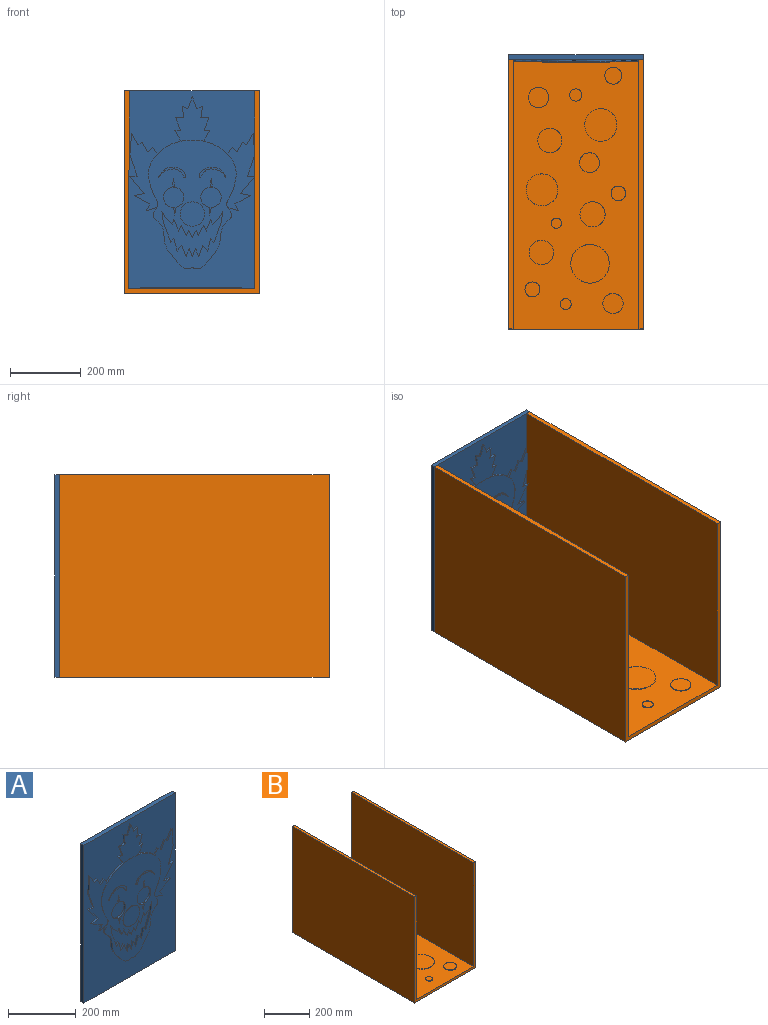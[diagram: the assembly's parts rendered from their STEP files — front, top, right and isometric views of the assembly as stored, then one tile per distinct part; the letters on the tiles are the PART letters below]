
ASSEMBLY  parts=2 mates=1
PART A: 117 faces, bbox 381x20.3x571.5 mm
  f0: plane 571.5x381mm, normal (0,-1,0), area 127557.7mm2, adj f1,f2,f3,f4,f37,f40,f42,f43
  f1: plane 381x12.7mm, normal (0,0,1), area 4838.7mm2, adj f0,f2,f4,f5
  f2: plane 571.5x12.7mm, normal (-1,0,0), area 7258mm2, adj f0,f1,f3,f5
  f3: plane 381x12.7mm, normal (0,0,-1), area 4838.7mm2, adj f0,f2,f4,f5
  f4: plane 571.5x12.7mm, normal (1,0,0), area 7258mm2, adj f0,f1,f3,f5
  f5: plane 571.5x381mm, normal (0,1,0), area 217741.5mm2, adj f1,f2,f3,f4
  f6: plane 19.84x18.99mm, normal (0.69,0,-0.72), area 174.4mm2, adj f7,f47,f48,f63
  f7: plane 17.73x9.29mm, normal (0.89,0,-0.46), area 127.1mm2, adj f6,f8,f48,f63
  f8: plane 32.08x6.35mm, normal (-0.99,0,0.12), area 205.1mm2, adj f7,f9,f48,f63
  f9: plane 56.13x21.1mm, normal (-0.94,0,0.35), area 380.8mm2, adj f8,f10,f48,f63
  f10: plane 10.13x8.86mm, normal (0.75,0,0.66), area 85.5mm2, adj f9,f11,f48,f63
  f11: plane 35.03x8.86mm, normal (-0.97,0,0.25), area 229.5mm2, adj f10,f12,f48,f63
  f12: plane 16.88x13.51mm, normal (0.78,0,0.62), area 137.3mm2, adj f11,f13,f48,f63
  f13: plane 32.5x11.82mm, normal (-0.94,0,0.34), area 219.6mm2, adj f12,f14,f48,f63
  f14: plane 22.37x8.44mm, normal (0.94,0,0.35), area 151.8mm2, adj f13,f15,f48,f63
  f15: plane 23.21x9.37mm, normal (-0.93,0,0.37), area 159mm2, adj f14,f16,f48,f63
  f16: plane 23.21x9.37mm, normal (0.93,0,0.37), area 159mm2, adj f15,f17,f48,f63
  f17: plane 22.37x8.44mm, normal (-0.94,0,0.35), area 151.8mm2, adj f16,f18,f48,f63
  f18: plane 32.5x11.82mm, normal (0.94,0,0.34), area 219.6mm2, adj f17,f19,f48,f63
  f19: plane 16.88x13.51mm, normal (-0.78,0,0.62), area 137.3mm2, adj f18,f20,f48,f63
  f20: plane 35.03x8.86mm, normal (0.97,0,0.25), area 229.5mm2, adj f19,f21,f48,f63
  f21: plane 10.13x8.86mm, normal (-0.75,0,0.66), area 85.5mm2, adj f20,f22,f48,f63
  f22: plane 56.13x21.1mm, normal (0.94,0,0.35), area 380.8mm2, adj f21,f23,f48,f63
  f23: plane 32.08x6.35mm, normal (0.99,0,0.12), area 205.1mm2, adj f22,f24,f48,f63
  f24: plane 17.73x9.29mm, normal (-0.89,0,-0.46), area 127.1mm2, adj f23,f25,f48,f63
  f25: plane 19.84x18.99mm, normal (-0.69,0,-0.72), area 174.4mm2, adj f24,f26,f48,f63
  f26: plane 13.96x6.35mm, normal (0.95,0,-0.32), area 93.7mm2, adj f25,f27,f48,f63
  f27: plane 33.84x12.78mm, normal (-0.94,0,-0.35), area 229.7mm2, adj f26,f28,f48,f63
  f28: plane 16.54x7.52mm, normal (0.91,0,-0.41), area 115.4mm2, adj f27,f29,f48,f63
  f29: plane 30.08x14.29mm, normal (-0.9,0,-0.43), area 211.5mm2, adj f28,f30,f48,f63
  f30: plane 15.79x6.77mm, normal (0.92,0,-0.39), area 109.1mm2, adj f29,f31,f48,f63
  f31: plane 20.3x10.51mm, normal (-0.89,0,-0.46), area 145.2mm2, adj f30,f32,f48,f63
  f32: plane 20.3x10.51mm, normal (0.89,0,-0.46), area 145.2mm2, adj f31,f33,f48,f63
  f33: plane 15.79x6.77mm, normal (-0.92,0,-0.39), area 109.1mm2, adj f32,f34,f48,f63
  f34: plane 30.08x14.29mm, normal (0.9,0,-0.43), area 211.5mm2, adj f33,f35,f48,f63
  f35: plane 16.54x7.52mm, normal (-0.91,0,-0.41), area 115.4mm2, adj f34,f36,f48,f63
  f36: plane 33.84x12.78mm, normal (0.94,0,-0.35), area 229.7mm2, adj f35,f47,f48,f63
  f37: extruded ~67.83x36.44mm, area 496.6mm2, adj f0,f38,f46,f48,f75,f104
  f38: extruded ~31.62x2.5mm, area 40.4mm2, adj f37,f39,f48,f88
  f39: extruded ~31.62x2.5mm, area 40.4mm2, adj f38,f40,f48,f88
  f40: extruded ~67.83x36.44mm, area 496.6mm2, adj f0,f39,f41,f48,f74,f89
  f41: extruded ~151.17x26.58mm, area 207.7mm2, adj f40,f42,f48,f102
  f42: extruded ~173.03x111.11mm, area 1449.8mm2, adj f0,f41,f43,f48,f101
  f43: extruded ~173.03x111.11mm, area 1449.8mm2, adj f0,f42,f46,f48,f105
  f44: cylinder r=28.78mm len=57.56mm, axis (0,1,0), area 1148.3mm2, adj f48,f65
  f45: cylinder r=28.78mm len=57.56mm, axis (0,1,0), area 1148.3mm2, adj f48,f64
  f46: extruded ~151.17x26.58mm, area 207.7mm2, adj f37,f43,f48,f116
  f47: plane 13.96x6.35mm, normal (-0.95,0,-0.32), area 93.7mm2, adj f6,f36,f48,f63
  f48: plane 367.53x249.86mm, normal (0,-1,0), area 47753.7mm2, adj f6,f7,f8,f9,f10,f11,f12,f13
  f49: plane 21.89x5.73mm, normal (0,-1,0), area 61.6mm2, adj f50,f51,f52
  f50: plane 21.22x2.46mm, normal (0.99,0,0.12), area 27.1mm2, adj f48,f49,f51,f52
  f51: plane 5.73x1.27mm, normal (0.12,0,-0.99), area 7.3mm2, adj f48,f49,f50,f52
  f52: plane 21.89x3.27mm, normal (-0.99,0,0.15), area 28.1mm2, adj f48,f49,f50,f51
  f53: plane 18.6x4.65mm, normal (0,-1,0), area 42.8mm2, adj f54,f55,f56
  f54: plane 18.6x1.27mm, normal (1,0,-0.06), area 23.7mm2, adj f48,f53,f55,f56
  f55: plane 17.91x3.48mm, normal (-0.98,0,-0.19), area 23.2mm2, adj f48,f53,f54,f56
  f56: plane 4.65x1.27mm, normal (-0.15,0,0.99), area 6mm2, adj f48,f53,f54,f55
  f57: plane 21.89x5.73mm, normal (0,-1,0), area 61.6mm2, adj f58,f59,f60
  f58: plane 5.73x1.27mm, normal (-0.12,0,-0.99), area 7.3mm2, adj f48,f57,f59,f60
  f59: plane 21.22x2.46mm, normal (-0.99,0,0.12), area 27.1mm2, adj f48,f57,f58,f60
  f60: plane 21.89x3.27mm, normal (0.99,0,0.15), area 28.1mm2, adj f48,f57,f58,f59
  f61: plane 69.41x69.41mm, normal (0,-1,0), area 3784.2mm2, adj f62
  f62: cylinder r=34.71mm len=69.41mm, axis (0,1,0), area 276.9mm2, adj f48,f61
  f63: plane 171.53x129.57mm, normal (0,-1,0), area 8466.9mm2, adj f6,f7,f8,f9,f10,f11,f12,f13
  f64: plane 57.56x57.56mm, normal (0,-1,0), area 2602.1mm2, adj f45
  f65: plane 57.56x57.56mm, normal (0,-1,0), area 2602.1mm2, adj f44
  f66: plane 77.58x32.72mm, normal (0,-1,0), area 463.6mm2, adj f67
  f67: extruded ~75.23x29.94mm, area 252.3mm2, adj f48,f66
  f68: plane 77.58x32.72mm, normal (0,-1,0), area 464.8mm2, adj f69
  f69: extruded ~75.23x29.94mm, area 252.3mm2, adj f48,f68
  f70: plane 18.6x4.65mm, normal (0,-1,0), area 42.8mm2, adj f71,f72,f73
  f71: plane 4.65x1.27mm, normal (0.15,0,0.99), area 6mm2, adj f48,f70,f72,f73
  f72: plane 17.91x3.48mm, normal (0.98,0,-0.19), area 23.2mm2, adj f48,f70,f71,f73
  f73: plane 18.6x1.27mm, normal (-1,0,-0.06), area 23.7mm2, adj f48,f70,f71,f72
  f74: plane 30.2x18.01mm, normal (-0.86,0,-0.51), area 178.6mm2, adj f0,f40,f87,f88
  f75: plane 30.2x18.01mm, normal (0.86,0,-0.51), area 178.6mm2, adj f0,f37,f76,f88
  f76: plane 16.18x5.08mm, normal (0,0,1), area 82.2mm2, adj f0,f75,f77,f88
  f77: plane 36.03x13.54mm, normal (0.94,0,-0.35), area 195.5mm2, adj f0,f76,f78,f88
  f78: plane 22.94x5.08mm, normal (0,0,1), area 116.5mm2, adj f0,f77,f79,f88
  f79: plane 32.34x5.08mm, normal (0.99,0,-0.15), area 166.1mm2, adj f0,f78,f80,f88
  f80: plane 16.54x6.77mm, normal (-0.38,0,0.93), area 90.8mm2, adj f0,f79,f81,f88
  f81: plane 33.46x12.39mm, normal (0.94,0,0.35), area 181.3mm2, adj f0,f80,f82,f88
  f82: plane 33.46x12.39mm, normal (-0.94,0,0.35), area 181.3mm2, adj f0,f81,f83,f88
  f83: plane 16.54x6.77mm, normal (0.38,0,0.93), area 90.8mm2, adj f0,f82,f84,f88
  f84: plane 32.34x5.08mm, normal (-0.99,0,-0.15), area 166.1mm2, adj f0,f83,f85,f88
  f85: plane 22.94x5.08mm, normal (0,0,1), area 116.5mm2, adj f0,f84,f86,f88
  f86: plane 36.03x13.54mm, normal (-0.94,0,-0.35), area 195.5mm2, adj f0,f85,f87,f88
  f87: plane 16.18x5.08mm, normal (0,0,1), area 82.2mm2, adj f0,f74,f86,f88
  f88: plane 125.26x99.25mm, normal (0,-1,0), area 7084.9mm2, adj f38,f39,f74,f75,f76,f77,f78,f79
  f89: plane 17.86x12.83mm, normal (0.81,0,0.58), area 111.7mm2, adj f0,f40,f90,f102
  f90: plane 14.6x11.87mm, normal (-0.63,0,0.78), area 95.6mm2, adj f0,f89,f91,f102
  f91: plane 27.04x14.65mm, normal (0.88,0,0.48), area 156.2mm2, adj f0,f90,f92,f102
  f92: plane 12.52x6.78mm, normal (-0.48,0,0.88), area 72.3mm2, adj f0,f91,f93,f102
  f93: plane 32.81x17.77mm, normal (0.88,0,0.48), area 189.6mm2, adj f0,f92,f94,f102
  f94: plane 61.52x5.08mm, normal (-1,0,0.08), area 313.4mm2, adj f0,f93,f95,f102
  f95: plane 59.72x20.28mm, normal (-0.95,0,-0.32), area 320.4mm2, adj f0,f94,f96,f102
  f96: plane 20.85x5.08mm, normal (0,0,1), area 105.9mm2, adj f0,f95,f97,f102
  f97: plane 49.58x41.13mm, normal (-0.77,0,-0.64), area 327.2mm2, adj f0,f96,f98,f102
  f98: plane 28.73x5.63mm, normal (-0.19,0,0.98), area 148.7mm2, adj f0,f97,f99,f102
  f99: plane 44.51x23.66mm, normal (-0.47,0,-0.88), area 256.1mm2, adj f0,f98,f100,f102
  f100: plane 18.9x10.05mm, normal (-0.88,0,0.47), area 108.8mm2, adj f0,f99,f101,f102
  f101: plane 29.51x8.79mm, normal (0.29,0,-0.96), area 156.4mm2, adj f0,f42,f100,f102
  f102: plane 219.02x81.12mm, normal (0,-1,0), area 8377.8mm2, adj f41,f89,f90,f91,f92,f93,f94,f95
  f103: plane 14.6x11.87mm, normal (0.63,0,0.78), area 95.6mm2, adj f0,f104,f115,f116
  f104: plane 17.86x12.83mm, normal (-0.81,0,0.58), area 111.7mm2, adj f0,f37,f103,f116
  f105: plane 29.51x8.79mm, normal (-0.29,0,-0.96), area 156.4mm2, adj f0,f43,f106,f116
  f106: plane 18.9x10.05mm, normal (0.88,0,0.47), area 108.8mm2, adj f0,f105,f107,f116
  f107: plane 44.51x23.66mm, normal (0.47,0,-0.88), area 256.1mm2, adj f0,f106,f108,f116
  f108: plane 28.73x5.63mm, normal (0.19,0,0.98), area 148.7mm2, adj f0,f107,f109,f116
  f109: plane 49.58x41.13mm, normal (0.77,0,-0.64), area 327.2mm2, adj f0,f108,f110,f116
  f110: plane 20.85x5.08mm, normal (0,0,1), area 105.9mm2, adj f0,f109,f111,f116
  f111: plane 59.72x20.28mm, normal (0.95,0,-0.32), area 320.4mm2, adj f0,f110,f112,f116
  f112: plane 61.52x5.08mm, normal (1,0,0.08), area 313.4mm2, adj f0,f111,f113,f116
  f113: plane 32.81x17.77mm, normal (-0.88,0,0.48), area 189.6mm2, adj f0,f112,f114,f116
  f114: plane 12.52x6.78mm, normal (0.48,0,0.88), area 72.3mm2, adj f0,f113,f115,f116
  f115: plane 27.04x14.65mm, normal (-0.88,0,0.48), area 156.2mm2, adj f0,f103,f114,f116
  f116: plane 219.02x81.12mm, normal (0,-1,0), area 8377.5mm2, adj f46,f103,f104,f105,f106,f107,f108,f109
PART B: 40 faces, bbox 381x762x571.5 mm
  f0: plane 762x12.7mm, normal (0,0,1), area 9677.4mm2, adj f1,f7,f8,f9
  f1: plane 762x571.5mm, normal (-1,0,0), area 435483mm2, adj f0,f2,f8,f9
  f2: plane 762x381mm, normal (0,0,-1), area 290322mm2, adj f1,f3,f8,f9
  f3: plane 762x571.5mm, normal (1,0,0), area 435483mm2, adj f2,f4,f8,f9
  f4: plane 762x12.7mm, normal (0,0,1), area 9677.4mm2, adj f3,f5,f8,f9
  f5: plane 762x558.8mm, normal (-1,0,0), area 425805.9mm2, adj f4,f6,f8,f9
  f6: plane 762x355.6mm, normal (0,0,1), area 222928.4mm2, adj f5,f7,f8,f9,f10,f12,f14,f16
  f7: plane 762x558.8mm, normal (1,0,0), area 425805.9mm2, adj f0,f6,f8,f9
  f8: plane 571.5x381mm, normal (0,1,0), area 19032.2mm2, adj f0,f1,f2,f3,f4,f5,f6,f7
  f9: plane 571.5x381mm, normal (0,-1,0), area 19032.2mm2, adj f0,f1,f2,f3,f4,f5,f6,f7
  f10: cylinder r=28.56mm len=57.12mm, axis (0,0,-1), area 455.8mm2, adj f6,f11
  f11: plane 57.12x57.12mm, normal (0,0,1), area 2562.1mm2, adj f10
  f12: cylinder r=45.7mm len=91.4mm, axis (0,0,-1), area 729.4mm2, adj f6,f13
  f13: plane 91.4x91.4mm, normal (0,0,1), area 6561.8mm2, adj f12
  f14: cylinder r=23.64mm len=47.28mm, axis (0,0,-1), area 377.3mm2, adj f6,f15
  f15: plane 47.28x47.28mm, normal (0,0,1), area 1756mm2, adj f14
  f16: cylinder r=34.24mm len=68.48mm, axis (0,0,-1), area 546.4mm2, adj f6,f17
  f17: plane 68.48x68.48mm, normal (0,0,1), area 3683.1mm2, adj f16
  f18: cylinder r=27.91mm len=55.82mm, axis (0,0,-1), area 445.4mm2, adj f6,f19
  f19: plane 55.82x55.82mm, normal (0,0,1), area 2447mm2, adj f18
  f20: cylinder r=45mm len=90mm, axis (0,0,-1), area 718.2mm2, adj f6,f21
  f21: plane 90x90mm, normal (0,0,1), area 6362.2mm2, adj f20
  f22: cylinder r=20.62mm len=41.24mm, axis (0,0,-1), area 329.1mm2, adj f6,f23
  f23: plane 41.24x41.24mm, normal (0,0,1), area 1335.7mm2, adj f22
  f24: cylinder r=35.53mm len=71.07mm, axis (0,0,-1), area 567.1mm2, adj f6,f25
  f25: plane 71.07x71.07mm, normal (0,0,1), area 3967mm2, adj f24
  f26: cylinder r=14.39mm len=28.78mm, axis (0,0,-1), area 229.7mm2, adj f6,f27
  f27: plane 28.78x28.78mm, normal (0,0,1), area 650.6mm2, adj f26
  f28: cylinder r=34.51mm len=69.03mm, axis (0,0,-1), area 550.8mm2, adj f6,f29
  f29: plane 69.03x69.03mm, normal (0,0,1), area 3742.4mm2, adj f28
  f30: cylinder r=54.49mm len=108.97mm, axis (0,0,-1), area 869.6mm2, adj f6,f31
  f31: plane 108.97x108.97mm, normal (0,0,1), area 9327mm2, adj f30
  f32: cylinder r=28.56mm len=57.12mm, axis (0,0,-1), area 455.8mm2, adj f6,f33
  f33: plane 57.12x57.12mm, normal (0,0,1), area 2562.1mm2, adj f32
  f34: cylinder r=15.44mm len=30.87mm, axis (0,0,-1), area 246.3mm2, adj f6,f35
  f35: plane 30.87x30.87mm, normal (0,0,1), area 748.5mm2, adj f34
  f36: cylinder r=21.06mm len=42.12mm, axis (0,0,-1), area 336.1mm2, adj f6,f37
  f37: plane 42.12x42.12mm, normal (0,0,1), area 1393.3mm2, adj f36
  f38: cylinder r=17.3mm len=34.6mm, axis (0,0,-1), area 276.1mm2, adj f6,f39
  f39: plane 34.6x34.6mm, normal (0,0,1), area 940mm2, adj f38
PLACE A t=(1.65,774.7,16.65)mm
PLACE B at identity
MATE fastened A.f3 <-> B.f2  axis (0,0,1) through (191.19,762,-281.47)mm
